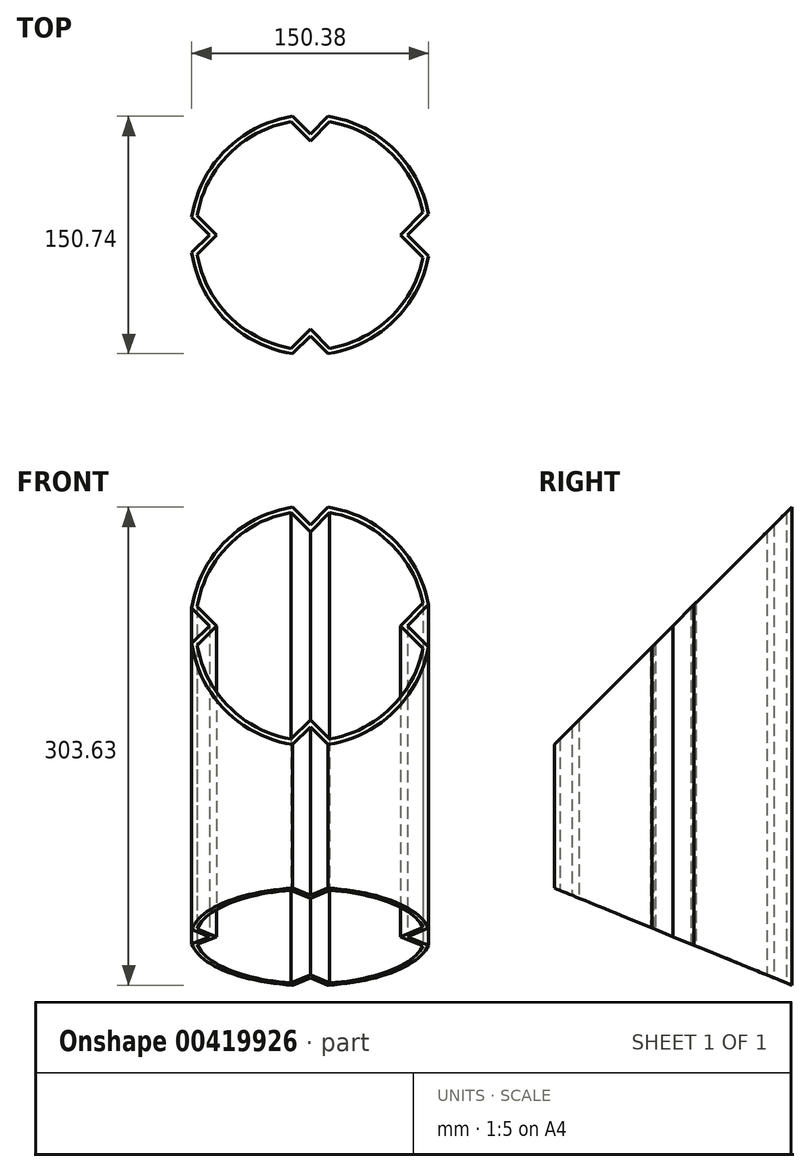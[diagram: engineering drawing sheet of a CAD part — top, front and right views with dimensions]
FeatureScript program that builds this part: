
annotation { "Feature Type Name" : "Feature", "Feature Type Description" : "" }
export const myFeature = defineFeature(function(context is Context, id is Id, definition is map)
    precondition{}
    {
        {
            var Q0;
            Q0=qCreatedBy(makeId("Top.planeOp"),FACE);
            var sketch = newSketch(context, id + "F0", { "sketchPlane" : qUnion([Q0])});
            skArc(sketch, "E0", {"start": v(-75.37, -11.23) * mm, "mid": v(-53.88, -53.88) * mm, "end": v(-11.23, -75.37) * mm});
            skArc(sketch, "E1.0", {"start": v(-71.98, -12.32) * mm, "mid": v(-51.64, -51.64) * mm, "end": v(-12.32, -71.98) * mm});
            skLineSegment(sketch, "E2", {"start": v(0, -64.14) * mm, "end": v(-11.23, -75.37) * mm});
            skLineSegment(sketch, "E3", {"start": v(0, -64.14) * mm, "end": v(11.23, -75.37) * mm});
            skLineSegment(sketch, "E4", {"start": v(-64.14, 0) * mm, "end": v(-75.37, 11.23) * mm});
            skLineSegment(sketch, "E5", {"start": v(-64.14, 0) * mm, "end": v(-75.37, -11.23) * mm});
            skLineSegment(sketch, "E6", {"start": v(0, 64.14) * mm, "end": v(-11.23, 75.37) * mm});
            skLineSegment(sketch, "E7", {"start": v(0, 64.14) * mm, "end": v(11.23, 75.37) * mm});
            skLineSegment(sketch, "E8", {"start": v(61.6, 0) * mm, "end": v(75.01, 13.4) * mm});
            skLineSegment(sketch, "E9", {"start": v(61.6, 0) * mm, "end": v(75.01, -13.4) * mm});
            skLineSegment(sketch, "E10", {"start": v(-71.98, 12.32) * mm, "end": v(-59.65, 0) * mm});
            skLineSegment(sketch, "E11", {"start": v(-59.65, 0) * mm, "end": v(-71.98, -12.32) * mm});
            skLineSegment(sketch, "E12", {"start": v(-12.32, 71.98) * mm, "end": v(0, 59.65) * mm});
            skLineSegment(sketch, "E13", {"start": v(0, 59.65) * mm, "end": v(12.32, 71.98) * mm});
            skLineSegment(sketch, "E14", {"start": v(71.58, 14.46) * mm, "end": v(57.11, 0) * mm});
            skLineSegment(sketch, "E15", {"start": v(57.11, 0) * mm, "end": v(71.58, -14.46) * mm});
            skLineSegment(sketch, "E16", {"start": v(-12.32, -71.98) * mm, "end": v(0, -59.65) * mm});
            skLineSegment(sketch, "E17", {"start": v(0, -59.65) * mm, "end": v(12.32, -71.98) * mm});
            skPoint(sketch, "E18.start.orphan", {"position": v(-76.2, 0) * mm});
            skArc(sketch, "E19.trimOffspring", {"start": v(12.32, -71.98) * mm, "mid": v(50.86, -52.4) * mm, "end": v(71.58, -14.46) * mm});
            skPoint(sketch, "E20.start.orphan", {"position": v(0, -76.2) * mm});
            skArc(sketch, "E21.trimOffspring", {"start": v(11.23, -75.37) * mm, "mid": v(53.1, -54.66) * mm, "end": v(75.01, -13.4) * mm});
            skArc(sketch, "E22.trimOffspring", {"start": v(75.01, 13.4) * mm, "mid": v(53.1, 54.66) * mm, "end": v(11.23, 75.37) * mm});
            skArc(sketch, "E23.trimOffspring", {"start": v(71.58, 14.46) * mm, "mid": v(50.86, 52.4) * mm, "end": v(12.32, 71.98) * mm});
            skPoint(sketch, "E24.orphan", {"position": v(76.2, 0) * mm});
            skPoint(sketch, "E25.orphan", {"position": v(0, 76.2) * mm});
            skArc(sketch, "E26.trimOffspring", {"start": v(-11.23, 75.37) * mm, "mid": v(-53.88, 53.88) * mm, "end": v(-75.37, 11.23) * mm});
            skArc(sketch, "E27.trimOffspring", {"start": v(-12.32, 71.98) * mm, "mid": v(-51.64, 51.64) * mm, "end": v(-71.98, 12.32) * mm});
            skSolve(sketch);
        }
        {
            var Q0;
            Q0 = qSketchRegion(id + "F0", true);
            extrude(context, id + "F1", {"entities" : qUnion([Q0]), "depth" : 304.8 * mm});
        }
        {
            var Q0;
            Q0=qCreatedBy(makeId("Right.planeOp"),FACE);
            var sketch = newSketch(context, id + "F2", { "sketchPlane" : qUnion([Q0])});
            skLineSegment(sketch, "E28.bottom", {"start": v(76.2, 304.8) * mm, "end": v(-76.2, 304.8) * mm});
            skLineSegment(sketch, "E28.left", {"start": v(76.2, 304.8) * mm, "end": v(76.2, 152.4) * mm});
            skLineSegment(sketch, "E28.right", {"start": v(-76.2, 304.8) * mm, "end": v(-76.2, 152.4) * mm});
            skPoint(sketch, "E28.middle", {"position": v(0, 228.6) * mm});
            skLineSegment(sketch, "E29.bottom", {"start": v(76.2, 0) * mm, "end": v(-76.2, 0) * mm});
            skLineSegment(sketch, "E29.left", {"start": v(76.2, 0) * mm, "end": v(76.2, 62.35) * mm});
            skLineSegment(sketch, "E29.right", {"start": v(-76.2, 0) * mm, "end": v(-76.2, 62.35) * mm});
            skPoint(sketch, "E29.middle", {"position": v(0, 31.17) * mm});
            skLineSegment(sketch, "E30", {"start": v(-76.2, 152.4) * mm, "end": v(76.2, 304.8) * mm});
            skLineSegment(sketch, "E31", {"start": v(-76.2, 62.35) * mm, "end": v(76.2, 0) * mm});
            skSolve(sketch);
        }
        {
            var Q0;
            Q0 = qSketchRegion(id + "F2", true);
            extrude(context, id + "F3", {"entities" : qUnion([Q0]), "operationType" : NewBodyOperationType.REMOVE, "endBound" : BoundingType.THROUGH_ALL, "oppositeDirection" : true, "depth" : 25.4 * mm, "hasSecondDirection" : true, "secondDirectionBound" : SecondDirectionBoundingType.THROUGH_ALL, "secondDirectionOppositeDirection" : false, "secondDirectionDepth" : 25.4 * mm});
        }
    });
